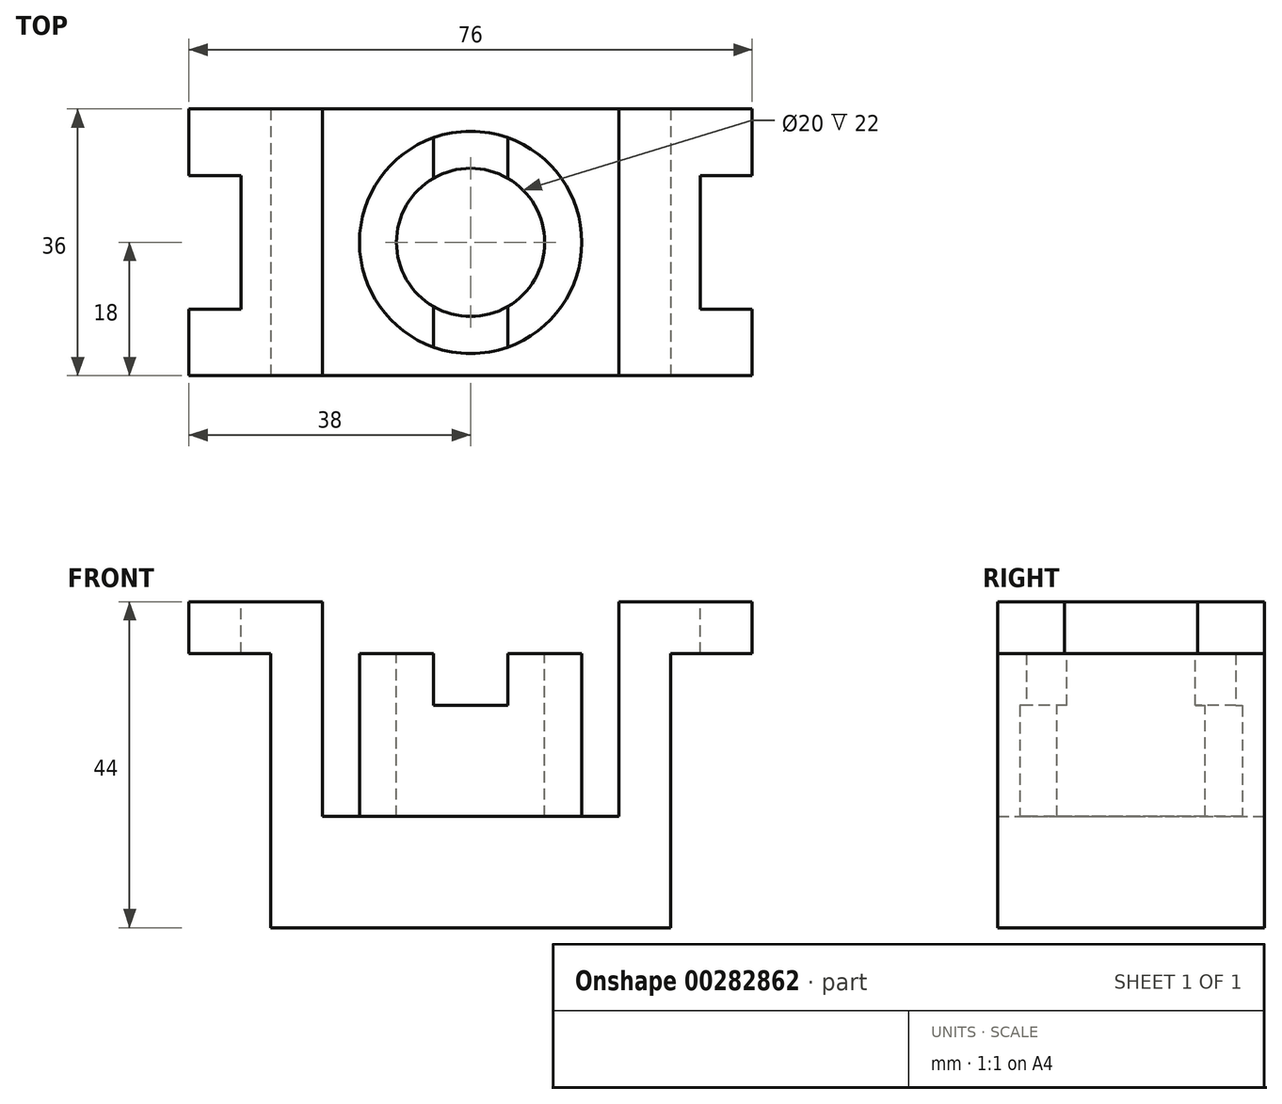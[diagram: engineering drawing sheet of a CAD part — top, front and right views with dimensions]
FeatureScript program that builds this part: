
annotation { "Feature Type Name" : "Feature", "Feature Type Description" : "" }
export const myFeature = defineFeature(function(context is Context, id is Id, definition is map)
    precondition{}
    {
        {
            var Q0;
            Q0=qCreatedBy(makeId("Front.planeOp"),FACE);
            var sketch = newSketch(context, id + "F0", { "sketchPlane" : qUnion([Q0])});
            skLineSegment(sketch, "E0.bottom", {"start": v(0, 0) * mm, "end": v(76, 0) * mm});
            skLineSegment(sketch, "E0.top", {"start": v(0, 44) * mm, "end": v(76, 44) * mm});
            skLineSegment(sketch, "E0.left", {"start": v(0, 0) * mm, "end": v(0, 44) * mm});
            skLineSegment(sketch, "E0.right", {"start": v(76, 0) * mm, "end": v(76, 44) * mm});
            skSolve(sketch);
        }
        {
            var Q0;
            Q0=makeQuery(id+"F0.imprint","IMPRINT",FACE,{"disambiguationData":[TD([[makeQuery(id+"F0.imprint","IMPRINT",EDGE,{"derivedFrom":sQuery(id+"F0.wireOp",EDGE,"E0.bottom")}),1.0]])]});
            extrude(context, id + "F1", {"entities" : qUnion([Q0]), "oppositeDirection" : true, "depth" : 36 * mm});
        }
        {
            var Q0;
            Q0=makeQuery(id+"F1.opExtrude","CAP_FACE",FACE,{"disambiguationData":[OSD([sQuery(id+"F0.wireOp",EDGE,"E0.bottom"),sQuery(id+"F0.wireOp",EDGE,"E0.top"),sQuery(id+"F0.wireOp",EDGE,"E0.left"),sQuery(id+"F0.wireOp",EDGE,"E0.right")])],"isStart":true});
            var sketch = newSketch(context, id + "F2", { "sketchPlane" : qUnion([Q0])});
            skLineSegment(sketch, "E1.bottom", {"start": v(0, 0) * mm, "end": v(11, 0) * mm});
            skLineSegment(sketch, "E1.top", {"start": v(0, 37) * mm, "end": v(11, 37) * mm});
            skLineSegment(sketch, "E1.left", {"start": v(0, 0) * mm, "end": v(0, 37) * mm});
            skLineSegment(sketch, "E1.right", {"start": v(11, 0) * mm, "end": v(11, 37) * mm});
            skLineSegment(sketch, "E2.bottom", {"start": v(76, 0) * mm, "end": v(65, 0) * mm});
            skLineSegment(sketch, "E2.top", {"start": v(76, 37) * mm, "end": v(65, 37) * mm});
            skLineSegment(sketch, "E2.left", {"start": v(76, 0) * mm, "end": v(76, 37) * mm});
            skLineSegment(sketch, "E2.right", {"start": v(65, 0) * mm, "end": v(65, 37) * mm});
            skSolve(sketch);
        }
        {
            var Q0;
            Q0=makeQuery(id+"F2.imprint","IMPRINT",FACE,{"disambiguationData":[TD([[makeQuery(id+"F2.imprint","IMPRINT",EDGE,{"derivedFrom":sQuery(id+"F2.wireOp",EDGE,"E1.bottom")}),1.0]])]});
            var Q1;
            Q1=makeQuery(id+"F2.imprint","IMPRINT",FACE,{"disambiguationData":[TD([[makeQuery(id+"F2.imprint","IMPRINT",EDGE,{"derivedFrom":sQuery(id+"F2.wireOp",EDGE,"E2.bottom")}),1.0]])]});
            extrude(context, id + "F3", {"entities" : qUnion([Q0, Q1]), "operationType" : NewBodyOperationType.REMOVE, "oppositeDirection" : true, "depth" : 36 * mm});
        }
        {
            var Q0;
            Q0=makeQuery(id+"F1.opExtrude","SWEPT_FACE",FACE,{"disambiguationData":[OSD([sQuery(id+"F0.wireOp",EDGE,"E0.top")])]});
            var sketch = newSketch(context, id + "F4", { "sketchPlane" : qUnion([Q0])});
            skLineSegment(sketch, "E3.top", {"start": v(0, 9) * mm, "end": v(7, 9) * mm});
            skLineSegment(sketch, "E4.top", {"start": v(7, 27) * mm, "end": v(0, 27) * mm});
            skLineSegment(sketch, "E4.left", {"start": v(7, 9) * mm, "end": v(7, 27) * mm});
            skLineSegment(sketch, "E4.right", {"start": v(0, 9) * mm, "end": v(0, 27) * mm});
            skLineSegment(sketch, "E5.top", {"start": v(76, 9) * mm, "end": v(69, 9) * mm});
            skLineSegment(sketch, "E6.top", {"start": v(76, 27) * mm, "end": v(69, 27) * mm});
            skLineSegment(sketch, "E6.left", {"start": v(76, 9) * mm, "end": v(76, 27) * mm});
            skLineSegment(sketch, "E6.right", {"start": v(69, 9) * mm, "end": v(69, 27) * mm});
            skLineSegment(sketch, "E7.bottom", {"start": v(18, 0) * mm, "end": v(58, 0) * mm});
            skLineSegment(sketch, "E7.top", {"start": v(18, 36) * mm, "end": v(58, 36) * mm});
            skLineSegment(sketch, "E7.left", {"start": v(18, 0) * mm, "end": v(18, 36) * mm});
            skLineSegment(sketch, "E7.right", {"start": v(58, 0) * mm, "end": v(58, 36) * mm});
            skSolve(sketch);
        }
        {
            var Q0;
            Q0=makeQuery(id+"F4.imprint","IMPRINT",FACE,{"disambiguationData":[TD([[makeQuery(id+"F4.imprint","IMPRINT",EDGE,{"derivedFrom":sQuery(id+"F4.wireOp",EDGE,"E5.top")}),-1.0]])]});
            var Q1;
            Q1=makeQuery(id+"F4.imprint","IMPRINT",FACE,{"disambiguationData":[TD([[makeQuery(id+"F4.imprint","IMPRINT",EDGE,{"derivedFrom":sQuery(id+"F4.wireOp",EDGE,"E7.bottom")}),1.0]])]});
            var Q2;
            Q2=makeQuery(id+"F4.imprint","IMPRINT",FACE,{"disambiguationData":[TD([[makeQuery(id+"F4.imprint","IMPRINT",EDGE,{"derivedFrom":sQuery(id+"F4.wireOp",EDGE,"E3.top")}),1.0]])]});
            extrude(context, id + "F5", {"entities" : qUnion([Q0, Q1, Q2]), "operationType" : NewBodyOperationType.REMOVE, "oppositeDirection" : true, "depth" : 29 * mm});
        }
        {
            var Q0;
            Q0=makeQuery(id+"F5.boolean.opBoolean","COPY",FACE,{"derivedFrom":makeQuery(id+"F5.opExtrude","CAP_FACE",FACE,{"disambiguationData":[OSD([sQuery(id+"F4.wireOp",EDGE,"E7.bottom"),sQuery(id+"F4.wireOp",EDGE,"E7.top"),sQuery(id+"F4.wireOp",EDGE,"E7.left"),sQuery(id+"F4.wireOp",EDGE,"E7.right")])],"isStart":false})});
            var sketch = newSketch(context, id + "F6", { "sketchPlane" : qUnion([Q0])});
            skCircle(sketch, "E8", {"center": v(38, 18) * mm, "radius": 15 * mm});
            skPoint(sketch, "E8.centerSnap0", {"position": v(18, 18) * mm});
            skPoint(sketch, "E8.centerSnap1", {"position": v(38, 0) * mm});
            skSolve(sketch);
        }
        {
            var Q0;
            Q0=makeQuery(id+"F6.imprint","IMPRINT",FACE,{"disambiguationData":[TD([[makeQuery(id+"F6.imprint","IMPRINT",EDGE,{"derivedFrom":sQuery(id+"F6.wireOp",EDGE,"E8")}),1.0]])]});
            extrude(context, id + "F7", {"entities" : qUnion([Q0]), "operationType" : NewBodyOperationType.ADD, "depth" : 22 * mm});
        }
        {
            var Q0;
            Q0=makeQuery(id+"F7.opExtrude","CAP_FACE",FACE,{"disambiguationData":[OSD([sQuery(id+"F6.wireOp",EDGE,"E8")])],"isStart":false});
            var sketch = newSketch(context, id + "F8", { "sketchPlane" : qUnion([Q0])});
            skLineSegment(sketch, "E9.bottom", {"start": v(38, 18) * mm, "end": v(43, 18) * mm});
            skLineSegment(sketch, "E9.top", {"start": v(38, 0) * mm, "end": v(43, 0) * mm});
            skLineSegment(sketch, "E9.left", {"start": v(38, 18) * mm, "end": v(38, 0) * mm});
            skLineSegment(sketch, "E9.right", {"start": v(43, 18) * mm, "end": v(43, 0) * mm});
            skLineSegment(sketch, "E10.bottom", {"start": v(43, 0) * mm, "end": v(33, 0) * mm});
            skLineSegment(sketch, "E10.top", {"start": v(43, 36) * mm, "end": v(33, 36) * mm});
            skLineSegment(sketch, "E10.left", {"start": v(43, 0) * mm, "end": v(43, 36) * mm});
            skLineSegment(sketch, "E10.right", {"start": v(33, 0) * mm, "end": v(33, 36) * mm});
            skSolve(sketch);
        }
        {
            var Q0;
            {var subQ0=sQuery(id+"F8.wireOp",EDGE,"E9.bottom");Q0=makeQuery(id+"F8.imprint","IMPRINT",FACE,{"disambiguationData":[TD([[makeQuery(id+"F8.imprint","IMPRINT",EDGE,{"derivedFrom":subQ0}),-1.0]])]});}
            var Q1;
            {var subQ1=sQuery(id+"F8.wireOp",EDGE,"E9.bottom");Q1=makeQuery(id+"F8.imprint","IMPRINT",FACE,{"disambiguationData":[TD([[makeQuery(id+"F8.imprint","IMPRINT",EDGE,{"derivedFrom":subQ1}),1.0]])]});}
            var Q2;
            {var subQ0=sQuery(id+"F8.wireOp",EDGE,"E10.top");Q2=makeQuery(id+"F8.imprint","IMPRINT",FACE,{"disambiguationData":[TD([[makeQuery(id+"F8.imprint","IMPRINT",EDGE,{"derivedFrom":subQ0}),1.0]])]});}
            var Q3;
            {var subQ0=sQuery(id+"F8.wireOp",EDGE,"E10.bottom");var subQ1=sQuery(id+"F8.wireOp",EDGE,"E9.left");var subQ2=makeQuery(id+"F8.imprint","INTERSECT",VERTEX,{"derivedFrom":[subQ1,subQ0]});Q3=makeQuery(id+"F8.imprint","IMPRINT",FACE,{"disambiguationData":[TD([[makeQuery(id+"F8.imprint","IMPRINT",EDGE,{"disambiguationData":[TD([[subQ2,1.0]])],"derivedFrom":subQ1}),1.0]])]});}
            var Q4;
            {var subQ0=sQuery(id+"F8.wireOp",EDGE,"E10.bottom");var subQ1=sQuery(id+"F8.wireOp",EDGE,"E9.left");var subQ2=makeQuery(id+"F8.imprint","INTERSECT",VERTEX,{"derivedFrom":[subQ1,subQ0]});Q4=makeQuery(id+"F8.imprint","IMPRINT",FACE,{"disambiguationData":[TD([[makeQuery(id+"F8.imprint","IMPRINT",EDGE,{"disambiguationData":[TD([[subQ2,1.0]])],"derivedFrom":subQ1}),-1.0]])]});}
            extrude(context, id + "F9", {"entities" : qUnion([Q0, Q1, Q2, Q3, Q4]), "operationType" : NewBodyOperationType.REMOVE, "oppositeDirection" : true, "depth" : 7 * mm});
        }
        {
            var Q0;
            {var subQ0=sQuery(id+"F6.wireOp",EDGE,"E8");Q0=makeQuery(id+"F9.boolean.opBoolean","SPLIT",FACE,{"disambiguationData":[TD([makeQuery(id+"F9.opExtrude","SWEPT_FACE",FACE,{"disambiguationData":[OSD([sQuery(id+"F8.wireOp",EDGE,"E10.right")])]})])],"derivedFrom":makeQuery(id+"F7.opExtrude","CAP_FACE",FACE,{"disambiguationData":[OSD([subQ0])],"isStart":false})});}
            var sketch = newSketch(context, id + "F10", { "sketchPlane" : qUnion([Q0])});
            skCircle(sketch, "E11", {"center": v(38, 18) * mm, "radius": 10 * mm});
            skSolve(sketch);
        }
        {
            var Q0;
            {var subQ0=sQuery(id+"F10.wireOp",EDGE,"E11");var subQ1=makeQuery(id+"F9.boolean.opBoolean","COPY",EDGE,{"derivedFrom":makeQuery(id+"F9.opExtrude","CAP_EDGE",EDGE,{"disambiguationData":[OSD([sQuery(id+"F8.wireOp",EDGE,"E10.right")])],"isStart":true})});var subQ2=makeQuery(id+"F10.imprint","INTERSECT",VERTEX,{"disambiguationData":[OD(0.0)],"derivedFrom":[subQ1,subQ0]});Q0=makeQuery(id+"F10.imprint","IMPRINT",FACE,{"disambiguationData":[TD([[makeQuery(id+"F10.imprint","IMPRINT",EDGE,{"disambiguationData":[TD([[subQ2,-1.0]])],"derivedFrom":subQ0}),1.0]])]});}
            var Q1;
            {var subQ0=sQuery(id+"F10.wireOp",EDGE,"E11");var subQ1=makeQuery(id+"F9.boolean.opBoolean","COPY",EDGE,{"derivedFrom":makeQuery(id+"F9.opExtrude","CAP_EDGE",EDGE,{"disambiguationData":[OSD([sQuery(id+"F8.wireOp",EDGE,"E10.right")])],"isStart":true})});var subQ2=makeQuery(id+"F10.imprint","INTERSECT",VERTEX,{"disambiguationData":[OD(0.0)],"derivedFrom":[subQ1,subQ0]});Q1=makeQuery(id+"F10.imprint","IMPRINT",FACE,{"disambiguationData":[TD([[makeQuery(id+"F10.imprint","IMPRINT",EDGE,{"disambiguationData":[TD([[subQ2,1.0]])],"derivedFrom":subQ0}),1.0]])]});}
            extrude(context, id + "F11", {"entities" : qUnion([Q0, Q1]), "operationType" : NewBodyOperationType.REMOVE, "oppositeDirection" : true, "depth" : 22 * mm});
        }
    });
